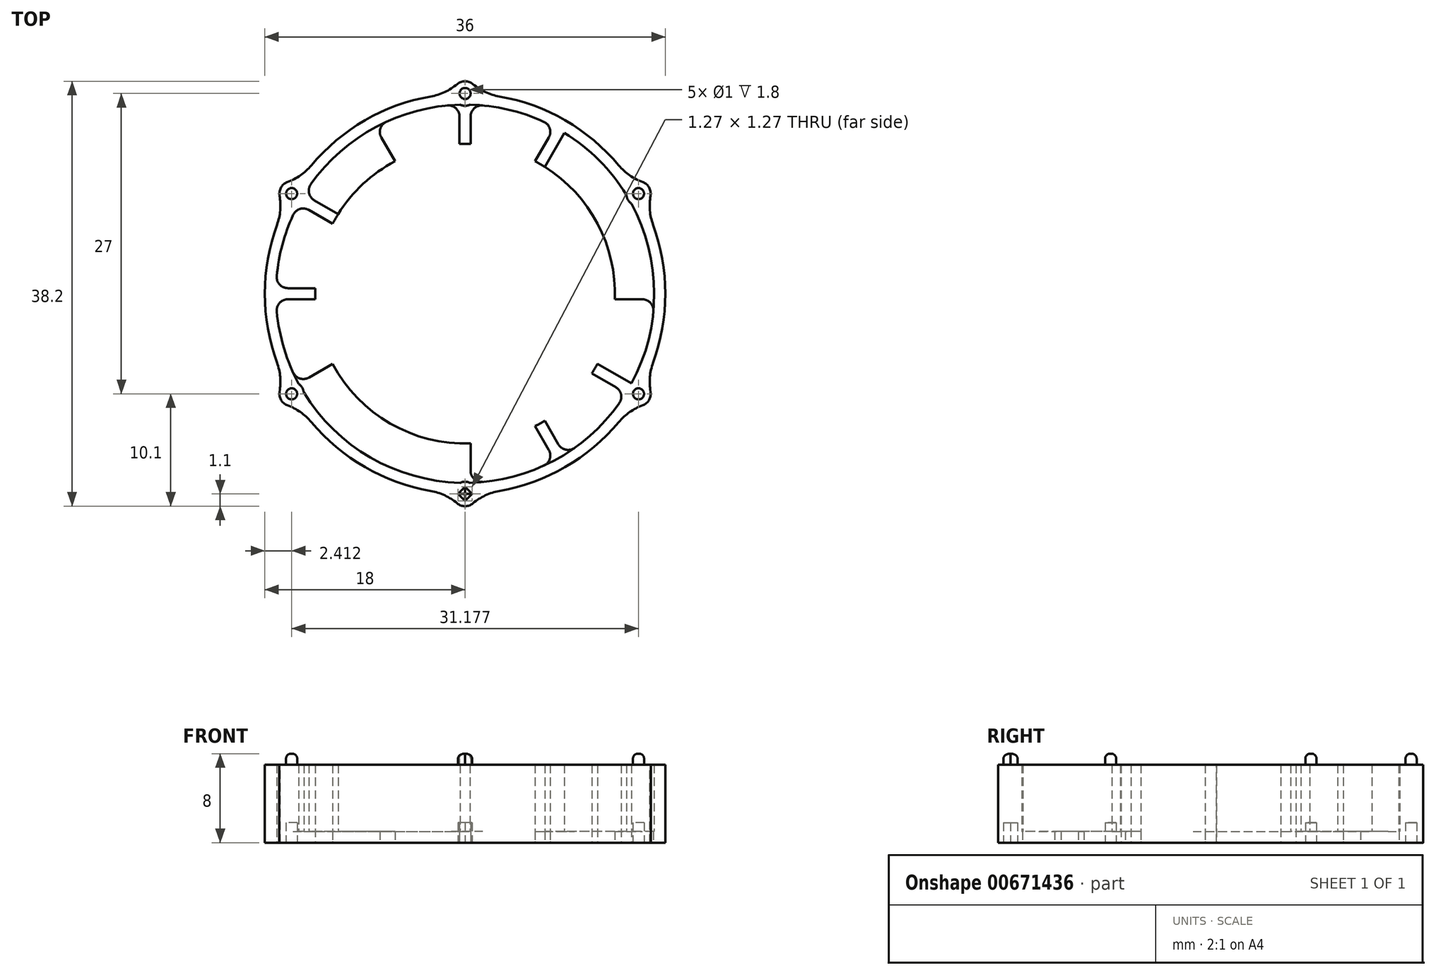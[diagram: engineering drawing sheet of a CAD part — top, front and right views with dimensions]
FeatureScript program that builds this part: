
annotation { "Feature Type Name" : "Feature", "Feature Type Description" : "" }
export const myFeature = defineFeature(function(context is Context, id is Id, definition is map)
    precondition{}
    {
        {
            var Q0;
            Q0=qCreatedBy(makeId("Top.planeOp"),FACE);
            var sketch = newSketch(context, id + "F0", { "sketchPlane" : qUnion([Q0])});
            skCircle(sketch, "E0", {"center": v(0, 0) * mm, "radius": 18 * mm});
            skCircle(sketch, "E1.0", {"center": v(0, 0) * mm, "radius": 17 * mm});
            skLineSegment(sketch, "E2.bottom", {"start": v(8.56, 15.83) * mm, "end": v(9.43, 15.33) * mm});
            skLineSegment(sketch, "E2.top", {"start": v(-9.43, -15.33) * mm, "end": v(-8.56, -15.83) * mm});
            skLineSegment(sketch, "E2.left", {"start": v(8.56, 15.83) * mm, "end": v(-9.43, -15.33) * mm});
            skLineSegment(sketch, "E2.right", {"start": v(9.43, 15.33) * mm, "end": v(-8.56, -15.83) * mm});
            skLineSegment(sketch, "E3.bottom", {"start": v(15.33, 9.43) * mm, "end": v(15.83, 8.56) * mm});
            skLineSegment(sketch, "E3.top", {"start": v(-15.83, -8.56) * mm, "end": v(-15.33, -9.43) * mm});
            skLineSegment(sketch, "E3.left", {"start": v(15.33, 9.43) * mm, "end": v(-15.83, -8.56) * mm});
            skLineSegment(sketch, "E3.right", {"start": v(15.83, 8.56) * mm, "end": v(-15.33, -9.43) * mm});
            skLineSegment(sketch, "E4", {"start": v(-38.35, 0) * mm, "end": v(39.17, 0) * mm, "construction": true});
            skLineSegment(sketch, "E5", {"start": v(0, 42.5) * mm, "end": v(0, -42.47) * mm, "construction": true});
            skLineSegment(sketch, "E6.bottom", {"start": v(-18, 0.5) * mm, "end": v(18, 0.5) * mm});
            skLineSegment(sketch, "E6.top", {"start": v(-18, -0.5) * mm, "end": v(18, -0.5) * mm});
            skLineSegment(sketch, "E6.left", {"start": v(-18, 0.5) * mm, "end": v(-18, -0.5) * mm});
            skLineSegment(sketch, "E6.right", {"start": v(18, 0.5) * mm, "end": v(18, -0.5) * mm});
            skLineSegment(sketch, "E7.bottom", {"start": v(-15.33, 9.43) * mm, "end": v(15.83, -8.56) * mm});
            skLineSegment(sketch, "E7.top", {"start": v(-15.83, 8.56) * mm, "end": v(15.33, -9.43) * mm});
            skLineSegment(sketch, "E7.left", {"start": v(-15.33, 9.43) * mm, "end": v(-15.83, 8.56) * mm});
            skLineSegment(sketch, "E7.right", {"start": v(15.83, -8.56) * mm, "end": v(15.33, -9.43) * mm});
            skLineSegment(sketch, "E8.bottom", {"start": v(-0.5, 18) * mm, "end": v(0.5, 18) * mm});
            skLineSegment(sketch, "E8.top", {"start": v(-0.5, -18) * mm, "end": v(0.5, -18) * mm});
            skLineSegment(sketch, "E8.left", {"start": v(-0.5, 18) * mm, "end": v(-0.5, -18) * mm});
            skLineSegment(sketch, "E8.right", {"start": v(0.5, 18) * mm, "end": v(0.5, -18) * mm});
            skLineSegment(sketch, "E9.bottom", {"start": v(-9.43, 15.33) * mm, "end": v(-8.56, 15.83) * mm});
            skLineSegment(sketch, "E9.top", {"start": v(8.56, -15.83) * mm, "end": v(9.43, -15.33) * mm});
            skLineSegment(sketch, "E9.left", {"start": v(-9.43, 15.33) * mm, "end": v(8.56, -15.83) * mm});
            skLineSegment(sketch, "E9.right", {"start": v(-8.56, 15.83) * mm, "end": v(9.43, -15.33) * mm});
            skCircle(sketch, "E10", {"center": v(0, 0) * mm, "radius": 13.47 * mm});
            skSolve(sketch);
        }
        {
            var Q0;
            Q0=qCreatedBy(makeId("Top.planeOp"),FACE);
            var sketch = newSketch(context, id + "F1", { "sketchPlane" : qUnion([Q0])});
            skCircle(sketch, "E11", {"center": v(0, 0) * mm, "radius": 18 * mm});
            skCircle(sketch, "E12", {"center": v(0, 0) * mm, "radius": 17 * mm});
            skSolve(sketch);
        }
        {
            var Q0;
            Q0=makeQuery(id+"F1.imprint","IMPRINT",FACE,{"disambiguationData":[TD([[makeQuery(id+"F1.imprint","IMPRINT",EDGE,{"derivedFrom":sQuery(id+"F1.wireOp",EDGE,"E11")}),1.0]])]});
            extrude(context, id + "F2", {"entities" : qUnion([Q0]), "depth" : 7 * mm, "offsetDistance" : 25 * mm});
        }
        {
            var Q0;
            {var subQ0=sQuery(id+"F0.wireOp",EDGE,"E7.bottom");var subQ1=sQuery(id+"F0.wireOp",EDGE,"E1.0");var subQ2=makeQuery(id+"F0.imprint","INTERSECT",VERTEX,{"disambiguationData":[OD(0.0)],"derivedFrom":[subQ1,subQ0]});Q0=makeQuery(id+"F0.imprint","IMPRINT",FACE,{"disambiguationData":[TD([[makeQuery(id+"F0.imprint","IMPRINT",EDGE,{"disambiguationData":[TD([[subQ2,-1.0]])],"derivedFrom":subQ1}),1.0]])]});}
            var Q1;
            {var subQ0=sQuery(id+"F0.wireOp",EDGE,"E2.right");var subQ1=sQuery(id+"F0.wireOp",EDGE,"E1.0");var subQ2=makeQuery(id+"F0.imprint","INTERSECT",VERTEX,{"disambiguationData":[OD(0.0)],"derivedFrom":[subQ1,subQ0]});Q1=makeQuery(id+"F0.imprint","IMPRINT",FACE,{"disambiguationData":[TD([[makeQuery(id+"F0.imprint","IMPRINT",EDGE,{"disambiguationData":[TD([[subQ2,-1.0]])],"derivedFrom":subQ1}),1.0]])]});}
            var Q2;
            {var subQ0=sQuery(id+"F0.wireOp",EDGE,"E7.top");var subQ1=sQuery(id+"F0.wireOp",EDGE,"E1.0");var subQ2=makeQuery(id+"F0.imprint","INTERSECT",VERTEX,{"disambiguationData":[OD(1.0)],"derivedFrom":[subQ1,subQ0]});Q2=makeQuery(id+"F0.imprint","IMPRINT",FACE,{"disambiguationData":[TD([[makeQuery(id+"F0.imprint","IMPRINT",EDGE,{"disambiguationData":[TD([[subQ2,-1.0]])],"derivedFrom":subQ1}),1.0]])]});}
            var Q3;
            {var subQ0=sQuery(id+"F0.wireOp",EDGE,"E6.bottom");var subQ1=sQuery(id+"F0.wireOp",EDGE,"E1.0");var subQ2=makeQuery(id+"F0.imprint","INTERSECT",VERTEX,{"disambiguationData":[OD(1.0)],"derivedFrom":[subQ1,subQ0]});Q3=makeQuery(id+"F0.imprint","IMPRINT",FACE,{"disambiguationData":[TD([[makeQuery(id+"F0.imprint","IMPRINT",EDGE,{"disambiguationData":[TD([[subQ2,-1.0]])],"derivedFrom":subQ1}),1.0]])]});}
            extrude(context, id + "F3", {"entities" : qUnion([Q0, Q1, Q2, Q3]), "operationType" : NewBodyOperationType.ADD, "depth" : 7 * mm, "offsetDistance" : 25 * mm});
        }
        {
            var Q0;
            Q0=makeQuery(id+"F1.imprint","IMPRINT",FACE,{"disambiguationData":[TD([[makeQuery(id+"F1.imprint","IMPRINT",EDGE,{"derivedFrom":sQuery(id+"F1.wireOp",EDGE,"E11")}),1.0]])]});
            var Q1;
            Q1=makeQuery(id+"F1.imprint","IMPRINT",FACE,{"disambiguationData":[TD([[makeQuery(id+"F1.imprint","IMPRINT",EDGE,{"derivedFrom":sQuery(id+"F1.wireOp",EDGE,"E12")}),1.0]])]});
            extrude(context, id + "F4", {"entities" : qUnion([Q0, Q1]), "operationType" : NewBodyOperationType.ADD, "depth" : 1 * mm, "offsetDistance" : 25 * mm});
        }
        {
            var Q0;
            Q0=qCreatedBy(makeId("Top.planeOp"),FACE);
            var sketch = newSketch(context, id + "F5", { "sketchPlane" : qUnion([Q0])});
            skCircle(sketch, "E13", {"center": v(0, 0) * mm, "radius": 18 * mm});
            skLineSegment(sketch, "E14", {"start": v(0, 18) * mm, "end": v(0, -18) * mm, "construction": true});
            skLineSegment(sketch, "E15", {"start": v(15.59, 9) * mm, "end": v(0, 0) * mm, "construction": true});
            skLineSegment(sketch, "E16", {"start": v(9, 15.59) * mm, "end": v(0, 0) * mm, "construction": true});
            skLineSegment(sketch, "E17", {"start": v(0, 0) * mm, "end": v(18, 0) * mm, "construction": true});
            skLineSegment(sketch, "E18", {"start": v(0, 0) * mm, "end": v(15.59, -9) * mm, "construction": true});
            skLineSegment(sketch, "E19", {"start": v(0, 0) * mm, "end": v(9, -15.59) * mm, "construction": true});
            skLineSegment(sketch, "E20", {"start": v(0, 0) * mm, "end": v(-9, 15.59) * mm, "construction": true});
            skLineSegment(sketch, "E21", {"start": v(0, 0) * mm, "end": v(-15.59, 9) * mm, "construction": true});
            skLineSegment(sketch, "E22", {"start": v(0, 0) * mm, "end": v(-18, 0) * mm, "construction": true});
            skLineSegment(sketch, "E23", {"start": v(0, 0) * mm, "end": v(-15.59, -9) * mm, "construction": true});
            skLineSegment(sketch, "E24", {"start": v(0, 0) * mm, "end": v(-9, -15.59) * mm, "construction": true});
            skCircle(sketch, "E25", {"center": v(0, 18) * mm, "radius": 1.1 * mm});
            skCircle(sketch, "E26", {"center": v(15.59, 9) * mm, "radius": 1.1 * mm});
            skCircle(sketch, "E27", {"center": v(15.59, -9) * mm, "radius": 1.1 * mm});
            skCircle(sketch, "E28", {"center": v(0, -18) * mm, "radius": 1.1 * mm});
            skCircle(sketch, "E29", {"center": v(-15.59, -9) * mm, "radius": 1.1 * mm});
            skCircle(sketch, "E30", {"center": v(-15.59, 9) * mm, "radius": 1.1 * mm});
            skCircle(sketch, "E31", {"center": v(-15.59, 9) * mm, "radius": 0.5 * mm});
            skCircle(sketch, "E32", {"center": v(0, 18) * mm, "radius": 0.5 * mm});
            skCircle(sketch, "E33", {"center": v(15.59, 9) * mm, "radius": 0.5 * mm});
            skCircle(sketch, "E34", {"center": v(15.59, -9) * mm, "radius": 0.5 * mm});
            skCircle(sketch, "E35", {"center": v(-15.59, -9) * mm, "radius": 0.5 * mm});
            skLineSegment(sketch, "E36.bottom", {"start": v(0.64, -18) * mm, "end": v(0, -18.64) * mm});
            skLineSegment(sketch, "E36.top", {"start": v(0, -17.36) * mm, "end": v(-0.64, -18) * mm});
            skLineSegment(sketch, "E36.left", {"start": v(0.64, -18) * mm, "end": v(0, -17.36) * mm});
            skLineSegment(sketch, "E36.right", {"start": v(0, -18.64) * mm, "end": v(-0.64, -18) * mm});
            skSolve(sketch);
        }
        {
            var Q0;
            {var subQ0=sQuery(id+"F5.wireOp",EDGE,"E30");var subQ1=sQuery(id+"F5.wireOp",EDGE,"E13");var subQ2=makeQuery(id+"F5.imprint","INTERSECT",VERTEX,{"disambiguationData":[OD(0.0)],"derivedFrom":[subQ1,subQ0]});Q0=makeQuery(id+"F5.imprint","IMPRINT",FACE,{"disambiguationData":[TD([[makeQuery(id+"F5.imprint","IMPRINT",EDGE,{"disambiguationData":[TD([[subQ2,-1.0]])],"derivedFrom":subQ1}),1.0]])]});}
            var Q1;
            {var subQ0=sQuery(id+"F5.wireOp",EDGE,"E30");var subQ1=sQuery(id+"F5.wireOp",EDGE,"E13");var subQ2=makeQuery(id+"F5.imprint","INTERSECT",VERTEX,{"disambiguationData":[OD(0.0)],"derivedFrom":[subQ1,subQ0]});Q1=makeQuery(id+"F5.imprint","IMPRINT",FACE,{"disambiguationData":[TD([[makeQuery(id+"F5.imprint","IMPRINT",EDGE,{"disambiguationData":[TD([[subQ2,-1.0]])],"derivedFrom":subQ1}),-1.0]])]});}
            var Q2;
            {var subQ0=sQuery(id+"F5.wireOp",EDGE,"E25");var subQ1=sQuery(id+"F5.wireOp",EDGE,"E13");var subQ2=makeQuery(id+"F5.imprint","INTERSECT",VERTEX,{"disambiguationData":[OD(0.0)],"derivedFrom":[subQ1,subQ0]});Q2=makeQuery(id+"F5.imprint","IMPRINT",FACE,{"disambiguationData":[TD([[makeQuery(id+"F5.imprint","IMPRINT",EDGE,{"disambiguationData":[TD([[subQ2,-1.0]])],"derivedFrom":subQ1}),1.0]])]});}
            var Q3;
            {var subQ0=sQuery(id+"F5.wireOp",EDGE,"E25");var subQ1=sQuery(id+"F5.wireOp",EDGE,"E13");var subQ2=makeQuery(id+"F5.imprint","INTERSECT",VERTEX,{"disambiguationData":[OD(0.0)],"derivedFrom":[subQ1,subQ0]});Q3=makeQuery(id+"F5.imprint","IMPRINT",FACE,{"disambiguationData":[TD([[makeQuery(id+"F5.imprint","IMPRINT",EDGE,{"disambiguationData":[TD([[subQ2,-1.0]])],"derivedFrom":subQ1}),-1.0]])]});}
            var Q4;
            {var subQ0=sQuery(id+"F5.wireOp",EDGE,"E26");var subQ1=sQuery(id+"F5.wireOp",EDGE,"E13");var subQ2=makeQuery(id+"F5.imprint","INTERSECT",VERTEX,{"disambiguationData":[OD(0.0)],"derivedFrom":[subQ1,subQ0]});Q4=makeQuery(id+"F5.imprint","IMPRINT",FACE,{"disambiguationData":[TD([[makeQuery(id+"F5.imprint","IMPRINT",EDGE,{"disambiguationData":[TD([[subQ2,-1.0]])],"derivedFrom":subQ1}),-1.0]])]});}
            var Q5;
            {var subQ0=sQuery(id+"F5.wireOp",EDGE,"E26");var subQ1=sQuery(id+"F5.wireOp",EDGE,"E13");var subQ2=makeQuery(id+"F5.imprint","INTERSECT",VERTEX,{"disambiguationData":[OD(0.0)],"derivedFrom":[subQ1,subQ0]});Q5=makeQuery(id+"F5.imprint","IMPRINT",FACE,{"disambiguationData":[TD([[makeQuery(id+"F5.imprint","IMPRINT",EDGE,{"disambiguationData":[TD([[subQ2,-1.0]])],"derivedFrom":subQ1}),1.0]])]});}
            var Q6;
            {var subQ0=sQuery(id+"F5.wireOp",EDGE,"E29");var subQ1=sQuery(id+"F5.wireOp",EDGE,"E13");var subQ2=makeQuery(id+"F5.imprint","INTERSECT",VERTEX,{"disambiguationData":[OD(0.0)],"derivedFrom":[subQ1,subQ0]});Q6=makeQuery(id+"F5.imprint","IMPRINT",FACE,{"disambiguationData":[TD([[makeQuery(id+"F5.imprint","IMPRINT",EDGE,{"disambiguationData":[TD([[subQ2,-1.0]])],"derivedFrom":subQ1}),1.0]])]});}
            var Q7;
            {var subQ0=sQuery(id+"F5.wireOp",EDGE,"E29");var subQ1=sQuery(id+"F5.wireOp",EDGE,"E13");var subQ2=makeQuery(id+"F5.imprint","INTERSECT",VERTEX,{"disambiguationData":[OD(0.0)],"derivedFrom":[subQ1,subQ0]});Q7=makeQuery(id+"F5.imprint","IMPRINT",FACE,{"disambiguationData":[TD([[makeQuery(id+"F5.imprint","IMPRINT",EDGE,{"disambiguationData":[TD([[subQ2,-1.0]])],"derivedFrom":subQ1}),-1.0]])]});}
            var Q8;
            {var subQ3=sQuery(id+"F5.wireOp",EDGE,"E13");var subQ5=sQuery(id+"F5.wireOp",EDGE,"E28");var subQ6=makeQuery(id+"F5.imprint","INTERSECT",VERTEX,{"disambiguationData":[OD(0.0)],"derivedFrom":[subQ3,subQ5]});Q8=makeQuery(id+"F5.imprint","IMPRINT",FACE,{"disambiguationData":[TD([[makeQuery(id+"F5.imprint","IMPRINT",EDGE,{"disambiguationData":[TD([[subQ6,-1.0]])],"derivedFrom":subQ3}),1.0]])]});}
            var Q9;
            {var subQ6=sQuery(id+"F5.wireOp",EDGE,"E36.bottom");Q9=makeQuery(id+"F5.imprint","IMPRINT",FACE,{"disambiguationData":[TD([[makeQuery(id+"F5.imprint","IMPRINT",EDGE,{"derivedFrom":subQ6}),1.0]])]});}
            var Q10;
            {var subQ0=sQuery(id+"F5.wireOp",EDGE,"E27");var subQ1=sQuery(id+"F5.wireOp",EDGE,"E13");var subQ2=makeQuery(id+"F5.imprint","INTERSECT",VERTEX,{"disambiguationData":[OD(0.0)],"derivedFrom":[subQ1,subQ0]});Q10=makeQuery(id+"F5.imprint","IMPRINT",FACE,{"disambiguationData":[TD([[makeQuery(id+"F5.imprint","IMPRINT",EDGE,{"disambiguationData":[TD([[subQ2,-1.0]])],"derivedFrom":subQ1}),-1.0]])]});}
            var Q11;
            {var subQ0=sQuery(id+"F5.wireOp",EDGE,"E27");var subQ1=sQuery(id+"F5.wireOp",EDGE,"E13");var subQ2=makeQuery(id+"F5.imprint","INTERSECT",VERTEX,{"disambiguationData":[OD(0.0)],"derivedFrom":[subQ1,subQ0]});Q11=makeQuery(id+"F5.imprint","IMPRINT",FACE,{"disambiguationData":[TD([[makeQuery(id+"F5.imprint","IMPRINT",EDGE,{"disambiguationData":[TD([[subQ2,-1.0]])],"derivedFrom":subQ1}),1.0]])]});}
            var Q12;
            {var subQ0=sQuery(id+"F5.wireOp",EDGE,"E31");var subQ1=sQuery(id+"F5.wireOp",EDGE,"E13");var subQ2=makeQuery(id+"F5.imprint","INTERSECT",VERTEX,{"disambiguationData":[OD(0.0)],"derivedFrom":[subQ1,subQ0]});Q12=makeQuery(id+"F5.imprint","IMPRINT",FACE,{"disambiguationData":[TD([[makeQuery(id+"F5.imprint","IMPRINT",EDGE,{"disambiguationData":[TD([[subQ2,-1.0]])],"derivedFrom":subQ1}),1.0]])]});}
            var Q13;
            {var subQ0=sQuery(id+"F5.wireOp",EDGE,"E31");var subQ1=sQuery(id+"F5.wireOp",EDGE,"E13");var subQ2=makeQuery(id+"F5.imprint","INTERSECT",VERTEX,{"disambiguationData":[OD(0.0)],"derivedFrom":[subQ1,subQ0]});Q13=makeQuery(id+"F5.imprint","IMPRINT",FACE,{"disambiguationData":[TD([[makeQuery(id+"F5.imprint","IMPRINT",EDGE,{"disambiguationData":[TD([[subQ2,-1.0]])],"derivedFrom":subQ1}),-1.0]])]});}
            var Q14;
            {var subQ0=sQuery(id+"F5.wireOp",EDGE,"E32");var subQ1=sQuery(id+"F5.wireOp",EDGE,"E13");var subQ2=makeQuery(id+"F5.imprint","INTERSECT",VERTEX,{"disambiguationData":[OD(0.0)],"derivedFrom":[subQ1,subQ0]});Q14=makeQuery(id+"F5.imprint","IMPRINT",FACE,{"disambiguationData":[TD([[makeQuery(id+"F5.imprint","IMPRINT",EDGE,{"disambiguationData":[TD([[subQ2,-1.0]])],"derivedFrom":subQ1}),-1.0]])]});}
            var Q15;
            {var subQ0=sQuery(id+"F5.wireOp",EDGE,"E32");var subQ1=sQuery(id+"F5.wireOp",EDGE,"E13");var subQ2=makeQuery(id+"F5.imprint","INTERSECT",VERTEX,{"disambiguationData":[OD(0.0)],"derivedFrom":[subQ1,subQ0]});Q15=makeQuery(id+"F5.imprint","IMPRINT",FACE,{"disambiguationData":[TD([[makeQuery(id+"F5.imprint","IMPRINT",EDGE,{"disambiguationData":[TD([[subQ2,-1.0]])],"derivedFrom":subQ1}),1.0]])]});}
            var Q16;
            {var subQ0=sQuery(id+"F5.wireOp",EDGE,"E33");var subQ1=sQuery(id+"F5.wireOp",EDGE,"E13");var subQ2=makeQuery(id+"F5.imprint","INTERSECT",VERTEX,{"disambiguationData":[OD(0.0)],"derivedFrom":[subQ1,subQ0]});Q16=makeQuery(id+"F5.imprint","IMPRINT",FACE,{"disambiguationData":[TD([[makeQuery(id+"F5.imprint","IMPRINT",EDGE,{"disambiguationData":[TD([[subQ2,-1.0]])],"derivedFrom":subQ1}),-1.0]])]});}
            var Q17;
            {var subQ0=sQuery(id+"F5.wireOp",EDGE,"E33");var subQ1=sQuery(id+"F5.wireOp",EDGE,"E13");var subQ2=makeQuery(id+"F5.imprint","INTERSECT",VERTEX,{"disambiguationData":[OD(0.0)],"derivedFrom":[subQ1,subQ0]});Q17=makeQuery(id+"F5.imprint","IMPRINT",FACE,{"disambiguationData":[TD([[makeQuery(id+"F5.imprint","IMPRINT",EDGE,{"disambiguationData":[TD([[subQ2,-1.0]])],"derivedFrom":subQ1}),1.0]])]});}
            var Q18;
            {var subQ0=sQuery(id+"F5.wireOp",EDGE,"E34");var subQ1=sQuery(id+"F5.wireOp",EDGE,"E13");var subQ2=makeQuery(id+"F5.imprint","INTERSECT",VERTEX,{"disambiguationData":[OD(0.0)],"derivedFrom":[subQ1,subQ0]});Q18=makeQuery(id+"F5.imprint","IMPRINT",FACE,{"disambiguationData":[TD([[makeQuery(id+"F5.imprint","IMPRINT",EDGE,{"disambiguationData":[TD([[subQ2,-1.0]])],"derivedFrom":subQ1}),-1.0]])]});}
            var Q19;
            {var subQ0=sQuery(id+"F5.wireOp",EDGE,"E34");var subQ1=sQuery(id+"F5.wireOp",EDGE,"E13");var subQ2=makeQuery(id+"F5.imprint","INTERSECT",VERTEX,{"disambiguationData":[OD(0.0)],"derivedFrom":[subQ1,subQ0]});Q19=makeQuery(id+"F5.imprint","IMPRINT",FACE,{"disambiguationData":[TD([[makeQuery(id+"F5.imprint","IMPRINT",EDGE,{"disambiguationData":[TD([[subQ2,-1.0]])],"derivedFrom":subQ1}),1.0]])]});}
            var Q20;
            {var subQ1=sQuery(id+"F5.wireOp",EDGE,"E36.bottom");Q20=makeQuery(id+"F5.imprint","IMPRINT",FACE,{"disambiguationData":[TD([[makeQuery(id+"F5.imprint","IMPRINT",EDGE,{"derivedFrom":subQ1}),-1.0]])]});}
            var Q21;
            {var subQ0=sQuery(id+"F5.wireOp",EDGE,"E35");var subQ1=sQuery(id+"F5.wireOp",EDGE,"E13");var subQ2=makeQuery(id+"F5.imprint","INTERSECT",VERTEX,{"disambiguationData":[OD(0.0)],"derivedFrom":[subQ1,subQ0]});Q21=makeQuery(id+"F5.imprint","IMPRINT",FACE,{"disambiguationData":[TD([[makeQuery(id+"F5.imprint","IMPRINT",EDGE,{"disambiguationData":[TD([[subQ2,-1.0]])],"derivedFrom":subQ1}),-1.0]])]});}
            var Q22;
            {var subQ0=sQuery(id+"F5.wireOp",EDGE,"E35");var subQ1=sQuery(id+"F5.wireOp",EDGE,"E13");var subQ2=makeQuery(id+"F5.imprint","INTERSECT",VERTEX,{"disambiguationData":[OD(0.0)],"derivedFrom":[subQ1,subQ0]});Q22=makeQuery(id+"F5.imprint","IMPRINT",FACE,{"disambiguationData":[TD([[makeQuery(id+"F5.imprint","IMPRINT",EDGE,{"disambiguationData":[TD([[subQ2,-1.0]])],"derivedFrom":subQ1}),1.0]])]});}
            var Q23;
            {var subQ0=sQuery(id+"F5.wireOp",EDGE,"E36.top");var subQ1=sQuery(id+"F5.wireOp",EDGE,"E13");var subQ2=makeQuery(id+"F5.imprint","INTERSECT",VERTEX,{"derivedFrom":[subQ1,subQ0]});Q23=makeQuery(id+"F5.imprint","IMPRINT",FACE,{"disambiguationData":[TD([[makeQuery(id+"F5.imprint","IMPRINT",EDGE,{"disambiguationData":[TD([[subQ2,-1.0]])],"derivedFrom":subQ1}),1.0]])]});}
            extrude(context, id + "F6", {"entities" : qUnion([Q0, Q1, Q2, Q3, Q4, Q5, Q6, Q7, Q8, Q9, Q10, Q11, Q12, Q13, Q14, Q15, Q16, Q17, Q18, Q19, Q20, Q21, Q22, Q23]), "operationType" : NewBodyOperationType.ADD, "depth" : 7 * mm, "offsetDistance" : 25 * mm});
        }
        {
            var Q0;
            {var subQ0=sQuery(id+"F0.wireOp",EDGE,"E8.right");var subQ1=sQuery(id+"F0.wireOp",EDGE,"E1.0");Q0=makeQuery(id+"F3.opExtrude","SWEPT_EDGE",EDGE,{"disambiguationData":[OSD([subQ1,subQ0]),TDD([makeQuery(id+"F0.imprint","INTERSECT",VERTEX,{"disambiguationData":[OD(1.0)],"derivedFrom":[subQ1,subQ0]})])]});}
            var Q1;
            {var subQ0=sQuery(id+"F0.wireOp",EDGE,"E2.left");var subQ1=sQuery(id+"F0.wireOp",EDGE,"E1.0");Q1=makeQuery(id+"F3.opExtrude","SWEPT_EDGE",EDGE,{"disambiguationData":[OSD([subQ1,subQ0]),TDD([makeQuery(id+"F0.imprint","INTERSECT",VERTEX,{"disambiguationData":[OD(1.0)],"derivedFrom":[subQ1,subQ0]})])]});}
            var Q2;
            {var subQ0=sQuery(id+"F0.wireOp",EDGE,"E3.left");var subQ1=sQuery(id+"F0.wireOp",EDGE,"E1.0");Q2=makeQuery(id+"F3.opExtrude","SWEPT_EDGE",EDGE,{"disambiguationData":[OSD([subQ1,subQ0]),TDD([makeQuery(id+"F0.imprint","INTERSECT",VERTEX,{"disambiguationData":[OD(1.0)],"derivedFrom":[subQ1,subQ0]})])]});}
            var Q3;
            {var subQ0=sQuery(id+"F0.wireOp",EDGE,"E6.bottom");var subQ1=sQuery(id+"F0.wireOp",EDGE,"E1.0");Q3=makeQuery(id+"F3.opExtrude","SWEPT_EDGE",EDGE,{"disambiguationData":[OSD([subQ1,subQ0]),TDD([makeQuery(id+"F0.imprint","INTERSECT",VERTEX,{"disambiguationData":[OD(1.0)],"derivedFrom":[subQ1,subQ0]})])]});}
            var Q4;
            {var subQ0=sQuery(id+"F0.wireOp",EDGE,"E9.right");var subQ1=sQuery(id+"F0.wireOp",EDGE,"E1.0");Q4=makeQuery(id+"F3.opExtrude","SWEPT_EDGE",EDGE,{"disambiguationData":[OSD([subQ1,subQ0]),TDD([makeQuery(id+"F0.imprint","INTERSECT",VERTEX,{"disambiguationData":[OD(1.0)],"derivedFrom":[subQ1,subQ0]})])]});}
            var Q5;
            {var subQ0=sQuery(id+"F0.wireOp",EDGE,"E7.bottom");var subQ1=sQuery(id+"F0.wireOp",EDGE,"E1.0");Q5=makeQuery(id+"F3.opExtrude","SWEPT_EDGE",EDGE,{"disambiguationData":[OSD([subQ1,subQ0]),TDD([makeQuery(id+"F0.imprint","INTERSECT",VERTEX,{"disambiguationData":[OD(1.0)],"derivedFrom":[subQ1,subQ0]})])]});}
            var Q6;
            {var subQ0=sQuery(id+"F0.wireOp",EDGE,"E8.left");var subQ1=sQuery(id+"F0.wireOp",EDGE,"E1.0");Q6=makeQuery(id+"F3.opExtrude","SWEPT_EDGE",EDGE,{"disambiguationData":[OSD([subQ1,subQ0]),TDD([makeQuery(id+"F0.imprint","INTERSECT",VERTEX,{"disambiguationData":[OD(0.0)],"derivedFrom":[subQ1,subQ0]})])]});}
            var Q7;
            {var subQ0=sQuery(id+"F0.wireOp",EDGE,"E2.left");var subQ1=sQuery(id+"F0.wireOp",EDGE,"E1.0");Q7=makeQuery(id+"F3.opExtrude","SWEPT_EDGE",EDGE,{"disambiguationData":[OSD([subQ1,subQ0]),TDD([makeQuery(id+"F0.imprint","INTERSECT",VERTEX,{"disambiguationData":[OD(0.0)],"derivedFrom":[subQ1,subQ0]})])]});}
            var Q8;
            {var subQ0=sQuery(id+"F0.wireOp",EDGE,"E3.left");var subQ1=sQuery(id+"F0.wireOp",EDGE,"E1.0");Q8=makeQuery(id+"F3.opExtrude","SWEPT_EDGE",EDGE,{"disambiguationData":[OSD([subQ1,subQ0]),TDD([makeQuery(id+"F0.imprint","INTERSECT",VERTEX,{"disambiguationData":[OD(0.0)],"derivedFrom":[subQ1,subQ0]})])]});}
            var Q9;
            {var subQ0=sQuery(id+"F0.wireOp",EDGE,"E6.top");var subQ1=sQuery(id+"F0.wireOp",EDGE,"E1.0");Q9=makeQuery(id+"F3.opExtrude","SWEPT_EDGE",EDGE,{"disambiguationData":[OSD([subQ1,subQ0]),TDD([makeQuery(id+"F0.imprint","INTERSECT",VERTEX,{"disambiguationData":[OD(1.0)],"derivedFrom":[subQ1,subQ0]})])]});}
            var Q10;
            {var subQ0=sQuery(id+"F0.wireOp",EDGE,"E7.top");var subQ1=sQuery(id+"F0.wireOp",EDGE,"E1.0");Q10=makeQuery(id+"F3.opExtrude","SWEPT_EDGE",EDGE,{"disambiguationData":[OSD([subQ1,subQ0]),TDD([makeQuery(id+"F0.imprint","INTERSECT",VERTEX,{"disambiguationData":[OD(0.0)],"derivedFrom":[subQ1,subQ0]})])]});}
            var Q11;
            {var subQ0=sQuery(id+"F0.wireOp",EDGE,"E6.top");var subQ1=sQuery(id+"F0.wireOp",EDGE,"E1.0");Q11=makeQuery(id+"F3.opExtrude","SWEPT_EDGE",EDGE,{"disambiguationData":[OSD([subQ1,subQ0]),TDD([makeQuery(id+"F0.imprint","INTERSECT",VERTEX,{"disambiguationData":[OD(0.0)],"derivedFrom":[subQ1,subQ0]})])]});}
            var Q12;
            {var subQ0=sQuery(id+"F0.wireOp",EDGE,"E9.left");var subQ1=sQuery(id+"F0.wireOp",EDGE,"E1.0");Q12=makeQuery(id+"F3.opExtrude","SWEPT_EDGE",EDGE,{"disambiguationData":[OSD([subQ1,subQ0]),TDD([makeQuery(id+"F0.imprint","INTERSECT",VERTEX,{"disambiguationData":[OD(0.0)],"derivedFrom":[subQ1,subQ0]})])]});}
            var Q13;
            {var subQ0=sQuery(id+"F0.wireOp",EDGE,"E8.right");var subQ1=sQuery(id+"F0.wireOp",EDGE,"E1.0");Q13=makeQuery(id+"F3.opExtrude","SWEPT_EDGE",EDGE,{"disambiguationData":[OSD([subQ1,subQ0]),TDD([makeQuery(id+"F0.imprint","INTERSECT",VERTEX,{"disambiguationData":[OD(0.0)],"derivedFrom":[subQ1,subQ0]})])]});}
            var Q14;
            {var subQ0=sQuery(id+"F0.wireOp",EDGE,"E7.bottom");var subQ1=sQuery(id+"F0.wireOp",EDGE,"E1.0");Q14=makeQuery(id+"F3.opExtrude","SWEPT_EDGE",EDGE,{"disambiguationData":[OSD([subQ1,subQ0]),TDD([makeQuery(id+"F0.imprint","INTERSECT",VERTEX,{"disambiguationData":[OD(0.0)],"derivedFrom":[subQ1,subQ0]})])]});}
            var Q15;
            {var subQ0=sQuery(id+"F0.wireOp",EDGE,"E9.right");var subQ1=sQuery(id+"F0.wireOp",EDGE,"E1.0");Q15=makeQuery(id+"F3.opExtrude","SWEPT_EDGE",EDGE,{"disambiguationData":[OSD([subQ1,subQ0]),TDD([makeQuery(id+"F0.imprint","INTERSECT",VERTEX,{"disambiguationData":[OD(0.0)],"derivedFrom":[subQ1,subQ0]})])]});}
            var Q16;
            {var subQ0=sQuery(id+"F0.wireOp",EDGE,"E3.right");var subQ1=sQuery(id+"F0.wireOp",EDGE,"E1.0");Q16=makeQuery(id+"F3.opExtrude","SWEPT_EDGE",EDGE,{"disambiguationData":[OSD([subQ1,subQ0]),TDD([makeQuery(id+"F0.imprint","INTERSECT",VERTEX,{"disambiguationData":[OD(1.0)],"derivedFrom":[subQ1,subQ0]})])]});}
            var Q17;
            {var subQ0=sQuery(id+"F0.wireOp",EDGE,"E2.right");var subQ1=sQuery(id+"F0.wireOp",EDGE,"E1.0");Q17=makeQuery(id+"F3.opExtrude","SWEPT_EDGE",EDGE,{"disambiguationData":[OSD([subQ1,subQ0]),TDD([makeQuery(id+"F0.imprint","INTERSECT",VERTEX,{"disambiguationData":[OD(1.0)],"derivedFrom":[subQ1,subQ0]})])]});}
            var Q18;
            {var subQ0=sQuery(id+"F0.wireOp",EDGE,"E3.right");var subQ1=sQuery(id+"F0.wireOp",EDGE,"E1.0");Q18=makeQuery(id+"F3.opExtrude","SWEPT_EDGE",EDGE,{"disambiguationData":[OSD([subQ1,subQ0]),TDD([makeQuery(id+"F0.imprint","INTERSECT",VERTEX,{"disambiguationData":[OD(0.0)],"derivedFrom":[subQ1,subQ0]})])]});}
            var Q19;
            {var subQ0=sQuery(id+"F0.wireOp",EDGE,"E2.right");var subQ1=sQuery(id+"F0.wireOp",EDGE,"E1.0");Q19=makeQuery(id+"F3.opExtrude","SWEPT_EDGE",EDGE,{"disambiguationData":[OSD([subQ1,subQ0]),TDD([makeQuery(id+"F0.imprint","INTERSECT",VERTEX,{"disambiguationData":[OD(0.0)],"derivedFrom":[subQ1,subQ0]})])]});}
            var Q20;
            {var subQ0=sQuery(id+"F0.wireOp",EDGE,"E8.left");var subQ1=sQuery(id+"F0.wireOp",EDGE,"E1.0");Q20=makeQuery(id+"F3.opExtrude","SWEPT_EDGE",EDGE,{"disambiguationData":[OSD([subQ1,subQ0]),TDD([makeQuery(id+"F0.imprint","INTERSECT",VERTEX,{"disambiguationData":[OD(1.0)],"derivedFrom":[subQ1,subQ0]})])]});}
            var Q21;
            {var subQ0=sQuery(id+"F0.wireOp",EDGE,"E9.left");var subQ1=sQuery(id+"F0.wireOp",EDGE,"E1.0");Q21=makeQuery(id+"F3.opExtrude","SWEPT_EDGE",EDGE,{"disambiguationData":[OSD([subQ1,subQ0]),TDD([makeQuery(id+"F0.imprint","INTERSECT",VERTEX,{"disambiguationData":[OD(1.0)],"derivedFrom":[subQ1,subQ0]})])]});}
            var Q22;
            {var subQ0=sQuery(id+"F0.wireOp",EDGE,"E7.top");var subQ1=sQuery(id+"F0.wireOp",EDGE,"E1.0");Q22=makeQuery(id+"F3.opExtrude","SWEPT_EDGE",EDGE,{"disambiguationData":[OSD([subQ1,subQ0]),TDD([makeQuery(id+"F0.imprint","INTERSECT",VERTEX,{"disambiguationData":[OD(1.0)],"derivedFrom":[subQ1,subQ0]})])]});}
            var Q23;
            {var subQ0=sQuery(id+"F0.wireOp",EDGE,"E6.bottom");var subQ1=sQuery(id+"F0.wireOp",EDGE,"E1.0");Q23=makeQuery(id+"F3.opExtrude","SWEPT_EDGE",EDGE,{"disambiguationData":[OSD([subQ1,subQ0]),TDD([makeQuery(id+"F0.imprint","INTERSECT",VERTEX,{"disambiguationData":[OD(0.0)],"derivedFrom":[subQ1,subQ0]})])]});}
            fillet(context, id + "F7", {"entities" : qUnion([Q0, Q1, Q2, Q3, Q4, Q5, Q6, Q7, Q8, Q9, Q10, Q11, Q12, Q13, Q14, Q15, Q16, Q17, Q18, Q19, Q20, Q21, Q22, Q23]), "radius" : 1 * mm, "tangentPropagation" : true, "allowEdgeOverflow" : false});
        }
        {
            var Q0;
            Q0=makeQuery(id+"F6.boolean.opBoolean","INTERSECT",EDGE,{"disambiguationData":[OD(0.0)],"derivedFrom":[makeQuery(id+"F2.opExtrude","SWEPT_FACE",FACE,{"disambiguationData":[OSD([sQuery(id+"F1.wireOp",EDGE,"E11")])]}),makeQuery(id+"F6.opExtrude","SWEPT_FACE",FACE,{"disambiguationData":[OSD([sQuery(id+"F5.wireOp",EDGE,"E30")])]})]});
            var Q1;
            Q1=makeQuery(id+"F6.boolean.opBoolean","INTERSECT",EDGE,{"disambiguationData":[OD(1.0)],"derivedFrom":[makeQuery(id+"F2.opExtrude","SWEPT_FACE",FACE,{"disambiguationData":[OSD([sQuery(id+"F1.wireOp",EDGE,"E11")])]}),makeQuery(id+"F6.opExtrude","SWEPT_FACE",FACE,{"disambiguationData":[OSD([sQuery(id+"F5.wireOp",EDGE,"E30")])]})]});
            var Q2;
            Q2=makeQuery(id+"F6.boolean.opBoolean","INTERSECT",EDGE,{"disambiguationData":[OD(1.0)],"derivedFrom":[makeQuery(id+"F2.opExtrude","SWEPT_FACE",FACE,{"disambiguationData":[OSD([sQuery(id+"F1.wireOp",EDGE,"E11")])]}),makeQuery(id+"F6.opExtrude","SWEPT_FACE",FACE,{"disambiguationData":[OSD([sQuery(id+"F5.wireOp",EDGE,"E25")])]})]});
            var Q3;
            Q3=makeQuery(id+"F6.boolean.opBoolean","INTERSECT",EDGE,{"disambiguationData":[OD(1.0)],"derivedFrom":[makeQuery(id+"F2.opExtrude","SWEPT_FACE",FACE,{"disambiguationData":[OSD([sQuery(id+"F1.wireOp",EDGE,"E11")])]}),makeQuery(id+"F6.opExtrude","SWEPT_FACE",FACE,{"disambiguationData":[OSD([sQuery(id+"F5.wireOp",EDGE,"E29")])]})]});
            var Q4;
            Q4=makeQuery(id+"F6.boolean.opBoolean","INTERSECT",EDGE,{"disambiguationData":[OD(0.0)],"derivedFrom":[makeQuery(id+"F2.opExtrude","SWEPT_FACE",FACE,{"disambiguationData":[OSD([sQuery(id+"F1.wireOp",EDGE,"E11")])]}),makeQuery(id+"F6.opExtrude","SWEPT_FACE",FACE,{"disambiguationData":[OSD([sQuery(id+"F5.wireOp",EDGE,"E29")])]})]});
            var Q5;
            Q5=makeQuery(id+"F6.boolean.opBoolean","INTERSECT",EDGE,{"disambiguationData":[OD(1.0)],"derivedFrom":[makeQuery(id+"F2.opExtrude","SWEPT_FACE",FACE,{"disambiguationData":[OSD([sQuery(id+"F1.wireOp",EDGE,"E11")])]}),makeQuery(id+"F6.opExtrude","SWEPT_FACE",FACE,{"disambiguationData":[OSD([sQuery(id+"F5.wireOp",EDGE,"E28")])]})]});
            var Q6;
            Q6=makeQuery(id+"F6.boolean.opBoolean","INTERSECT",EDGE,{"disambiguationData":[OD(0.0)],"derivedFrom":[makeQuery(id+"F2.opExtrude","SWEPT_FACE",FACE,{"disambiguationData":[OSD([sQuery(id+"F1.wireOp",EDGE,"E11")])]}),makeQuery(id+"F6.opExtrude","SWEPT_FACE",FACE,{"disambiguationData":[OSD([sQuery(id+"F5.wireOp",EDGE,"E28")])]})]});
            var Q7;
            Q7=makeQuery(id+"F6.boolean.opBoolean","INTERSECT",EDGE,{"disambiguationData":[OD(1.0)],"derivedFrom":[makeQuery(id+"F2.opExtrude","SWEPT_FACE",FACE,{"disambiguationData":[OSD([sQuery(id+"F1.wireOp",EDGE,"E11")])]}),makeQuery(id+"F6.opExtrude","SWEPT_FACE",FACE,{"disambiguationData":[OSD([sQuery(id+"F5.wireOp",EDGE,"E27")])]})]});
            var Q8;
            Q8=makeQuery(id+"F6.boolean.opBoolean","INTERSECT",EDGE,{"disambiguationData":[OD(0.0)],"derivedFrom":[makeQuery(id+"F2.opExtrude","SWEPT_FACE",FACE,{"disambiguationData":[OSD([sQuery(id+"F1.wireOp",EDGE,"E11")])]}),makeQuery(id+"F6.opExtrude","SWEPT_FACE",FACE,{"disambiguationData":[OSD([sQuery(id+"F5.wireOp",EDGE,"E27")])]})]});
            var Q9;
            Q9=makeQuery(id+"F6.boolean.opBoolean","INTERSECT",EDGE,{"disambiguationData":[OD(1.0)],"derivedFrom":[makeQuery(id+"F2.opExtrude","SWEPT_FACE",FACE,{"disambiguationData":[OSD([sQuery(id+"F1.wireOp",EDGE,"E11")])]}),makeQuery(id+"F6.opExtrude","SWEPT_FACE",FACE,{"disambiguationData":[OSD([sQuery(id+"F5.wireOp",EDGE,"E26")])]})]});
            var Q10;
            Q10=makeQuery(id+"F6.boolean.opBoolean","INTERSECT",EDGE,{"disambiguationData":[OD(0.0)],"derivedFrom":[makeQuery(id+"F2.opExtrude","SWEPT_FACE",FACE,{"disambiguationData":[OSD([sQuery(id+"F1.wireOp",EDGE,"E11")])]}),makeQuery(id+"F6.opExtrude","SWEPT_FACE",FACE,{"disambiguationData":[OSD([sQuery(id+"F5.wireOp",EDGE,"E26")])]})]});
            var Q11;
            Q11=makeQuery(id+"F6.boolean.opBoolean","INTERSECT",EDGE,{"disambiguationData":[OD(0.0)],"derivedFrom":[makeQuery(id+"F2.opExtrude","SWEPT_FACE",FACE,{"disambiguationData":[OSD([sQuery(id+"F1.wireOp",EDGE,"E11")])]}),makeQuery(id+"F6.opExtrude","SWEPT_FACE",FACE,{"disambiguationData":[OSD([sQuery(id+"F5.wireOp",EDGE,"E25")])]})]});
            fillet(context, id + "F8", {"entities" : qUnion([Q0, Q1, Q2, Q3, Q4, Q5, Q6, Q7, Q8, Q9, Q10, Q11]), "radius" : 5 * mm, "tangentPropagation" : true, "allowEdgeOverflow" : false});
        }
        {
            var Q0;
            {var subQ0=sQuery(id+"F5.wireOp",EDGE,"E31");var subQ1=sQuery(id+"F5.wireOp",EDGE,"E13");var subQ2=makeQuery(id+"F5.imprint","INTERSECT",VERTEX,{"disambiguationData":[OD(0.0)],"derivedFrom":[subQ1,subQ0]});Q0=makeQuery(id+"F5.imprint","IMPRINT",FACE,{"disambiguationData":[TD([[makeQuery(id+"F5.imprint","IMPRINT",EDGE,{"disambiguationData":[TD([[subQ2,-1.0]])],"derivedFrom":subQ1}),-1.0]])]});}
            var Q1;
            {var subQ0=sQuery(id+"F5.wireOp",EDGE,"E31");var subQ1=sQuery(id+"F5.wireOp",EDGE,"E13");var subQ2=makeQuery(id+"F5.imprint","INTERSECT",VERTEX,{"disambiguationData":[OD(0.0)],"derivedFrom":[subQ1,subQ0]});Q1=makeQuery(id+"F5.imprint","IMPRINT",FACE,{"disambiguationData":[TD([[makeQuery(id+"F5.imprint","IMPRINT",EDGE,{"disambiguationData":[TD([[subQ2,-1.0]])],"derivedFrom":subQ1}),1.0]])]});}
            var Q2;
            {var subQ0=sQuery(id+"F5.wireOp",EDGE,"E32");var subQ1=sQuery(id+"F5.wireOp",EDGE,"E13");var subQ2=makeQuery(id+"F5.imprint","INTERSECT",VERTEX,{"disambiguationData":[OD(0.0)],"derivedFrom":[subQ1,subQ0]});Q2=makeQuery(id+"F5.imprint","IMPRINT",FACE,{"disambiguationData":[TD([[makeQuery(id+"F5.imprint","IMPRINT",EDGE,{"disambiguationData":[TD([[subQ2,-1.0]])],"derivedFrom":subQ1}),-1.0]])]});}
            var Q3;
            {var subQ0=sQuery(id+"F5.wireOp",EDGE,"E32");var subQ1=sQuery(id+"F5.wireOp",EDGE,"E13");var subQ2=makeQuery(id+"F5.imprint","INTERSECT",VERTEX,{"disambiguationData":[OD(0.0)],"derivedFrom":[subQ1,subQ0]});Q3=makeQuery(id+"F5.imprint","IMPRINT",FACE,{"disambiguationData":[TD([[makeQuery(id+"F5.imprint","IMPRINT",EDGE,{"disambiguationData":[TD([[subQ2,-1.0]])],"derivedFrom":subQ1}),1.0]])]});}
            var Q4;
            {var subQ0=sQuery(id+"F5.wireOp",EDGE,"E33");var subQ1=sQuery(id+"F5.wireOp",EDGE,"E13");var subQ2=makeQuery(id+"F5.imprint","INTERSECT",VERTEX,{"disambiguationData":[OD(0.0)],"derivedFrom":[subQ1,subQ0]});Q4=makeQuery(id+"F5.imprint","IMPRINT",FACE,{"disambiguationData":[TD([[makeQuery(id+"F5.imprint","IMPRINT",EDGE,{"disambiguationData":[TD([[subQ2,-1.0]])],"derivedFrom":subQ1}),1.0]])]});}
            var Q5;
            {var subQ0=sQuery(id+"F5.wireOp",EDGE,"E33");var subQ1=sQuery(id+"F5.wireOp",EDGE,"E13");var subQ2=makeQuery(id+"F5.imprint","INTERSECT",VERTEX,{"disambiguationData":[OD(0.0)],"derivedFrom":[subQ1,subQ0]});Q5=makeQuery(id+"F5.imprint","IMPRINT",FACE,{"disambiguationData":[TD([[makeQuery(id+"F5.imprint","IMPRINT",EDGE,{"disambiguationData":[TD([[subQ2,-1.0]])],"derivedFrom":subQ1}),-1.0]])]});}
            var Q6;
            {var subQ0=sQuery(id+"F5.wireOp",EDGE,"E34");var subQ1=sQuery(id+"F5.wireOp",EDGE,"E13");var subQ2=makeQuery(id+"F5.imprint","INTERSECT",VERTEX,{"disambiguationData":[OD(0.0)],"derivedFrom":[subQ1,subQ0]});Q6=makeQuery(id+"F5.imprint","IMPRINT",FACE,{"disambiguationData":[TD([[makeQuery(id+"F5.imprint","IMPRINT",EDGE,{"disambiguationData":[TD([[subQ2,-1.0]])],"derivedFrom":subQ1}),1.0]])]});}
            var Q7;
            {var subQ0=sQuery(id+"F5.wireOp",EDGE,"E34");var subQ1=sQuery(id+"F5.wireOp",EDGE,"E13");var subQ2=makeQuery(id+"F5.imprint","INTERSECT",VERTEX,{"disambiguationData":[OD(0.0)],"derivedFrom":[subQ1,subQ0]});Q7=makeQuery(id+"F5.imprint","IMPRINT",FACE,{"disambiguationData":[TD([[makeQuery(id+"F5.imprint","IMPRINT",EDGE,{"disambiguationData":[TD([[subQ2,-1.0]])],"derivedFrom":subQ1}),-1.0]])]});}
            var Q8;
            {var subQ1=sQuery(id+"F5.wireOp",EDGE,"E36.bottom");Q8=makeQuery(id+"F5.imprint","IMPRINT",FACE,{"disambiguationData":[TD([[makeQuery(id+"F5.imprint","IMPRINT",EDGE,{"derivedFrom":subQ1}),-1.0]])]});}
            var Q9;
            {var subQ0=sQuery(id+"F5.wireOp",EDGE,"E36.top");var subQ1=sQuery(id+"F5.wireOp",EDGE,"E13");var subQ2=makeQuery(id+"F5.imprint","INTERSECT",VERTEX,{"derivedFrom":[subQ1,subQ0]});Q9=makeQuery(id+"F5.imprint","IMPRINT",FACE,{"disambiguationData":[TD([[makeQuery(id+"F5.imprint","IMPRINT",EDGE,{"disambiguationData":[TD([[subQ2,-1.0]])],"derivedFrom":subQ1}),1.0]])]});}
            var Q10;
            {var subQ0=sQuery(id+"F5.wireOp",EDGE,"E35");var subQ1=sQuery(id+"F5.wireOp",EDGE,"E13");var subQ2=makeQuery(id+"F5.imprint","INTERSECT",VERTEX,{"disambiguationData":[OD(0.0)],"derivedFrom":[subQ1,subQ0]});Q10=makeQuery(id+"F5.imprint","IMPRINT",FACE,{"disambiguationData":[TD([[makeQuery(id+"F5.imprint","IMPRINT",EDGE,{"disambiguationData":[TD([[subQ2,-1.0]])],"derivedFrom":subQ1}),-1.0]])]});}
            var Q11;
            {var subQ0=sQuery(id+"F5.wireOp",EDGE,"E35");var subQ1=sQuery(id+"F5.wireOp",EDGE,"E13");var subQ2=makeQuery(id+"F5.imprint","INTERSECT",VERTEX,{"disambiguationData":[OD(0.0)],"derivedFrom":[subQ1,subQ0]});Q11=makeQuery(id+"F5.imprint","IMPRINT",FACE,{"disambiguationData":[TD([[makeQuery(id+"F5.imprint","IMPRINT",EDGE,{"disambiguationData":[TD([[subQ2,-1.0]])],"derivedFrom":subQ1}),1.0]])]});}
            extrude(context, id + "F9", {"entities" : qUnion([Q0, Q1, Q2, Q3, Q4, Q5, Q6, Q7, Q8, Q9, Q10, Q11]), "operationType" : NewBodyOperationType.ADD, "depth" : 8 * mm, "offsetDistance" : 25 * mm});
        }
        {
            var Q0;
            Q0=makeQuery(id+"F9.opExtrude","CAP_EDGE",EDGE,{"disambiguationData":[OSD([sQuery(id+"F5.wireOp",EDGE,"E35")])],"isStart":false});
            var Q1;
            Q1=makeQuery(id+"F9.opExtrude","CAP_FACE",FACE,{"disambiguationData":[OSD([sQuery(id+"F5.wireOp",EDGE,"E31")])],"isStart":false});
            var Q2;
            Q2=makeQuery(id+"F9.opExtrude","CAP_FACE",FACE,{"disambiguationData":[OSD([sQuery(id+"F5.wireOp",EDGE,"E32")])],"isStart":false});
            var Q3;
            Q3=makeQuery(id+"F9.opExtrude","CAP_FACE",FACE,{"disambiguationData":[OSD([sQuery(id+"F5.wireOp",EDGE,"E33")])],"isStart":false});
            var Q4;
            Q4=makeQuery(id+"F9.opExtrude","CAP_FACE",FACE,{"disambiguationData":[OSD([sQuery(id+"F5.wireOp",EDGE,"E34")])],"isStart":false});
            var Q5;
            Q5=makeQuery(id+"F9.opExtrude","CAP_EDGE",EDGE,{"disambiguationData":[OSD([sQuery(id+"F5.wireOp",EDGE,"E36.left")])],"isStart":false});
            var Q6;
            Q6=makeQuery(id+"F9.opExtrude","CAP_EDGE",EDGE,{"disambiguationData":[OSD([sQuery(id+"F5.wireOp",EDGE,"E36.right")])],"isStart":false});
            var Q7;
            Q7=makeQuery(id+"F9.opExtrude","CAP_EDGE",EDGE,{"disambiguationData":[OSD([sQuery(id+"F5.wireOp",EDGE,"E36.bottom")])],"isStart":false});
            var Q8;
            Q8=makeQuery(id+"F9.opExtrude","CAP_EDGE",EDGE,{"disambiguationData":[OSD([sQuery(id+"F5.wireOp",EDGE,"E36.top")])],"isStart":false});
            fillet(context, id + "F10", {"entities" : qUnion([Q0, Q1, Q2, Q3, Q4, Q5, Q6, Q7, Q8]), "radius" : .45 * mm, "tangentPropagation" : true, "allowEdgeOverflow" : false});
        }
        {
            var Q0;
            {var subQ0=sQuery(id+"F5.wireOp",EDGE,"E35");var subQ1=sQuery(id+"F5.wireOp",EDGE,"E13");var subQ2=makeQuery(id+"F5.imprint","INTERSECT",VERTEX,{"disambiguationData":[OD(0.0)],"derivedFrom":[subQ1,subQ0]});Q0=makeQuery(id+"F5.imprint","IMPRINT",FACE,{"disambiguationData":[TD([[makeQuery(id+"F5.imprint","IMPRINT",EDGE,{"disambiguationData":[TD([[subQ2,-1.0]])],"derivedFrom":subQ1}),-1.0]])]});}
            var Q1;
            {var subQ0=sQuery(id+"F5.wireOp",EDGE,"E35");var subQ1=sQuery(id+"F5.wireOp",EDGE,"E13");var subQ2=makeQuery(id+"F5.imprint","INTERSECT",VERTEX,{"disambiguationData":[OD(0.0)],"derivedFrom":[subQ1,subQ0]});Q1=makeQuery(id+"F5.imprint","IMPRINT",FACE,{"disambiguationData":[TD([[makeQuery(id+"F5.imprint","IMPRINT",EDGE,{"disambiguationData":[TD([[subQ2,-1.0]])],"derivedFrom":subQ1}),1.0]])]});}
            var Q2;
            {var subQ1=sQuery(id+"F5.wireOp",EDGE,"E36.bottom");Q2=makeQuery(id+"F5.imprint","IMPRINT",FACE,{"disambiguationData":[TD([[makeQuery(id+"F5.imprint","IMPRINT",EDGE,{"derivedFrom":subQ1}),-1.0]])]});}
            var Q3;
            {var subQ0=sQuery(id+"F5.wireOp",EDGE,"E36.top");var subQ1=sQuery(id+"F5.wireOp",EDGE,"E13");var subQ2=makeQuery(id+"F5.imprint","INTERSECT",VERTEX,{"derivedFrom":[subQ1,subQ0]});Q3=makeQuery(id+"F5.imprint","IMPRINT",FACE,{"disambiguationData":[TD([[makeQuery(id+"F5.imprint","IMPRINT",EDGE,{"disambiguationData":[TD([[subQ2,-1.0]])],"derivedFrom":subQ1}),1.0]])]});}
            var Q4;
            {var subQ0=sQuery(id+"F5.wireOp",EDGE,"E34");var subQ1=sQuery(id+"F5.wireOp",EDGE,"E13");var subQ2=makeQuery(id+"F5.imprint","INTERSECT",VERTEX,{"disambiguationData":[OD(0.0)],"derivedFrom":[subQ1,subQ0]});Q4=makeQuery(id+"F5.imprint","IMPRINT",FACE,{"disambiguationData":[TD([[makeQuery(id+"F5.imprint","IMPRINT",EDGE,{"disambiguationData":[TD([[subQ2,-1.0]])],"derivedFrom":subQ1}),1.0]])]});}
            var Q5;
            {var subQ0=sQuery(id+"F5.wireOp",EDGE,"E34");var subQ1=sQuery(id+"F5.wireOp",EDGE,"E13");var subQ2=makeQuery(id+"F5.imprint","INTERSECT",VERTEX,{"disambiguationData":[OD(0.0)],"derivedFrom":[subQ1,subQ0]});Q5=makeQuery(id+"F5.imprint","IMPRINT",FACE,{"disambiguationData":[TD([[makeQuery(id+"F5.imprint","IMPRINT",EDGE,{"disambiguationData":[TD([[subQ2,-1.0]])],"derivedFrom":subQ1}),-1.0]])]});}
            var Q6;
            {var subQ0=sQuery(id+"F5.wireOp",EDGE,"E33");var subQ1=sQuery(id+"F5.wireOp",EDGE,"E13");var subQ2=makeQuery(id+"F5.imprint","INTERSECT",VERTEX,{"disambiguationData":[OD(0.0)],"derivedFrom":[subQ1,subQ0]});Q6=makeQuery(id+"F5.imprint","IMPRINT",FACE,{"disambiguationData":[TD([[makeQuery(id+"F5.imprint","IMPRINT",EDGE,{"disambiguationData":[TD([[subQ2,-1.0]])],"derivedFrom":subQ1}),1.0]])]});}
            var Q7;
            {var subQ0=sQuery(id+"F5.wireOp",EDGE,"E33");var subQ1=sQuery(id+"F5.wireOp",EDGE,"E13");var subQ2=makeQuery(id+"F5.imprint","INTERSECT",VERTEX,{"disambiguationData":[OD(0.0)],"derivedFrom":[subQ1,subQ0]});Q7=makeQuery(id+"F5.imprint","IMPRINT",FACE,{"disambiguationData":[TD([[makeQuery(id+"F5.imprint","IMPRINT",EDGE,{"disambiguationData":[TD([[subQ2,-1.0]])],"derivedFrom":subQ1}),-1.0]])]});}
            var Q8;
            {var subQ0=sQuery(id+"F5.wireOp",EDGE,"E32");var subQ1=sQuery(id+"F5.wireOp",EDGE,"E13");var subQ2=makeQuery(id+"F5.imprint","INTERSECT",VERTEX,{"disambiguationData":[OD(0.0)],"derivedFrom":[subQ1,subQ0]});Q8=makeQuery(id+"F5.imprint","IMPRINT",FACE,{"disambiguationData":[TD([[makeQuery(id+"F5.imprint","IMPRINT",EDGE,{"disambiguationData":[TD([[subQ2,-1.0]])],"derivedFrom":subQ1}),1.0]])]});}
            var Q9;
            {var subQ0=sQuery(id+"F5.wireOp",EDGE,"E32");var subQ1=sQuery(id+"F5.wireOp",EDGE,"E13");var subQ2=makeQuery(id+"F5.imprint","INTERSECT",VERTEX,{"disambiguationData":[OD(0.0)],"derivedFrom":[subQ1,subQ0]});Q9=makeQuery(id+"F5.imprint","IMPRINT",FACE,{"disambiguationData":[TD([[makeQuery(id+"F5.imprint","IMPRINT",EDGE,{"disambiguationData":[TD([[subQ2,-1.0]])],"derivedFrom":subQ1}),-1.0]])]});}
            var Q10;
            {var subQ0=sQuery(id+"F5.wireOp",EDGE,"E31");var subQ1=sQuery(id+"F5.wireOp",EDGE,"E13");var subQ2=makeQuery(id+"F5.imprint","INTERSECT",VERTEX,{"disambiguationData":[OD(0.0)],"derivedFrom":[subQ1,subQ0]});Q10=makeQuery(id+"F5.imprint","IMPRINT",FACE,{"disambiguationData":[TD([[makeQuery(id+"F5.imprint","IMPRINT",EDGE,{"disambiguationData":[TD([[subQ2,-1.0]])],"derivedFrom":subQ1}),-1.0]])]});}
            var Q11;
            {var subQ0=sQuery(id+"F5.wireOp",EDGE,"E31");var subQ1=sQuery(id+"F5.wireOp",EDGE,"E13");var subQ2=makeQuery(id+"F5.imprint","INTERSECT",VERTEX,{"disambiguationData":[OD(0.0)],"derivedFrom":[subQ1,subQ0]});Q11=makeQuery(id+"F5.imprint","IMPRINT",FACE,{"disambiguationData":[TD([[makeQuery(id+"F5.imprint","IMPRINT",EDGE,{"disambiguationData":[TD([[subQ2,-1.0]])],"derivedFrom":subQ1}),1.0]])]});}
            extrude(context, id + "F11", {"entities" : qUnion([Q0, Q1, Q2, Q3, Q4, Q5, Q6, Q7, Q8, Q9, Q10, Q11]), "operationType" : NewBodyOperationType.REMOVE, "depth" : 1.8 * mm, "offsetDistance" : 25 * mm});
        }
        {
            var Q0;
            Q0=qCreatedBy(makeId("Top.planeOp"),FACE);
            var sketch = newSketch(context, id + "F12", { "sketchPlane" : qUnion([Q0])});
            skCircle(sketch, "E37", {"center": v(0, 0) * mm, "radius": 13.47 * mm});
            skSolve(sketch);
        }
        {
            var Q0;
            Q0=makeQuery(id+"F12.imprint","IMPRINT",FACE,{"disambiguationData":[TD([[makeQuery(id+"F12.imprint","IMPRINT",EDGE,{"derivedFrom":sQuery(id+"F12.wireOp",EDGE,"E37")}),1.0]])]});
            extrude(context, id + "F13", {"entities" : qUnion([Q0]), "operationType" : NewBodyOperationType.REMOVE, "depth" : 1 * mm, "offsetDistance" : 25 * mm});
        }
        {
            var Q0;
            {var subQ0=sQuery(id+"F0.wireOp",EDGE,"E8.right");var subQ1=sQuery(id+"F0.wireOp",EDGE,"E1.0");var subQ2=makeQuery(id+"F0.imprint","INTERSECT",VERTEX,{"disambiguationData":[OD(1.0)],"derivedFrom":[subQ1,subQ0]});Q0=makeQuery(id+"F0.imprint","IMPRINT",FACE,{"disambiguationData":[TD([[makeQuery(id+"F0.imprint","IMPRINT",EDGE,{"disambiguationData":[TD([[subQ2,-1.0]])],"derivedFrom":subQ1}),1.0]])]});}
            var Q1;
            {var subQ0=sQuery(id+"F0.wireOp",EDGE,"E9.right");var subQ1=sQuery(id+"F0.wireOp",EDGE,"E1.0");var subQ2=makeQuery(id+"F0.imprint","INTERSECT",VERTEX,{"disambiguationData":[OD(1.0)],"derivedFrom":[subQ1,subQ0]});Q1=makeQuery(id+"F0.imprint","IMPRINT",FACE,{"disambiguationData":[TD([[makeQuery(id+"F0.imprint","IMPRINT",EDGE,{"disambiguationData":[TD([[subQ2,-1.0]])],"derivedFrom":subQ1}),1.0]])]});}
            var Q2;
            {var subQ0=sQuery(id+"F0.wireOp",EDGE,"E7.bottom");var subQ1=sQuery(id+"F0.wireOp",EDGE,"E1.0");var subQ2=makeQuery(id+"F0.imprint","INTERSECT",VERTEX,{"disambiguationData":[OD(1.0)],"derivedFrom":[subQ1,subQ0]});Q2=makeQuery(id+"F0.imprint","IMPRINT",FACE,{"disambiguationData":[TD([[makeQuery(id+"F0.imprint","IMPRINT",EDGE,{"disambiguationData":[TD([[subQ2,-1.0]])],"derivedFrom":subQ1}),1.0]])]});}
            var Q3;
            {var subQ0=sQuery(id+"F0.wireOp",EDGE,"E2.left");var subQ1=sQuery(id+"F0.wireOp",EDGE,"E1.0");var subQ2=makeQuery(id+"F0.imprint","INTERSECT",VERTEX,{"disambiguationData":[OD(0.0)],"derivedFrom":[subQ1,subQ0]});Q3=makeQuery(id+"F0.imprint","IMPRINT",FACE,{"disambiguationData":[TD([[makeQuery(id+"F0.imprint","IMPRINT",EDGE,{"disambiguationData":[TD([[subQ2,-1.0]])],"derivedFrom":subQ1}),1.0]])]});}
            var Q4;
            {var subQ0=sQuery(id+"F0.wireOp",EDGE,"E8.left");var subQ1=sQuery(id+"F0.wireOp",EDGE,"E1.0");var subQ2=makeQuery(id+"F0.imprint","INTERSECT",VERTEX,{"disambiguationData":[OD(0.0)],"derivedFrom":[subQ1,subQ0]});Q4=makeQuery(id+"F0.imprint","IMPRINT",FACE,{"disambiguationData":[TD([[makeQuery(id+"F0.imprint","IMPRINT",EDGE,{"disambiguationData":[TD([[subQ2,-1.0]])],"derivedFrom":subQ1}),1.0]])]});}
            var Q5;
            {var subQ0=sQuery(id+"F0.wireOp",EDGE,"E7.top");var subQ1=sQuery(id+"F0.wireOp",EDGE,"E1.0");var subQ2=makeQuery(id+"F0.imprint","INTERSECT",VERTEX,{"disambiguationData":[OD(0.0)],"derivedFrom":[subQ1,subQ0]});Q5=makeQuery(id+"F0.imprint","IMPRINT",FACE,{"disambiguationData":[TD([[makeQuery(id+"F0.imprint","IMPRINT",EDGE,{"disambiguationData":[TD([[subQ2,-1.0]])],"derivedFrom":subQ1}),1.0]])]});}
            var Q6;
            {var subQ0=sQuery(id+"F0.wireOp",EDGE,"E6.top");var subQ1=sQuery(id+"F0.wireOp",EDGE,"E1.0");var subQ2=makeQuery(id+"F0.imprint","INTERSECT",VERTEX,{"disambiguationData":[OD(0.0)],"derivedFrom":[subQ1,subQ0]});Q6=makeQuery(id+"F0.imprint","IMPRINT",FACE,{"disambiguationData":[TD([[makeQuery(id+"F0.imprint","IMPRINT",EDGE,{"disambiguationData":[TD([[subQ2,-1.0]])],"derivedFrom":subQ1}),1.0]])]});}
            extrude(context, id + "F14", {"entities" : qUnion([Q0, Q1, Q2, Q3, Q4, Q5, Q6]), "operationType" : NewBodyOperationType.REMOVE, "depth" : 1 * mm, "offsetDistance" : 25 * mm});
        }
        {
            var Q0;
            {var subQ0=sQuery(id+"F0.wireOp",EDGE,"E6.top");var subQ1=sQuery(id+"F0.wireOp",EDGE,"E1.0");Q0=makeQuery(id+"F14.boolean.opBoolean","COPY",EDGE,{"derivedFrom":makeQuery(id+"F14.opExtrude","SWEPT_EDGE",EDGE,{"disambiguationData":[OSD([subQ1,subQ0]),TDD([makeQuery(id+"F0.imprint","INTERSECT",VERTEX,{"disambiguationData":[OD(0.0)],"derivedFrom":[subQ1,subQ0]})])]})});}
            var Q1;
            {var subQ0=sQuery(id+"F0.wireOp",EDGE,"E7.top");var subQ1=sQuery(id+"F0.wireOp",EDGE,"E1.0");Q1=makeQuery(id+"F14.boolean.opBoolean","COPY",EDGE,{"derivedFrom":makeQuery(id+"F14.opExtrude","SWEPT_EDGE",EDGE,{"disambiguationData":[OSD([subQ1,subQ0]),TDD([makeQuery(id+"F0.imprint","INTERSECT",VERTEX,{"disambiguationData":[OD(0.0)],"derivedFrom":[subQ1,subQ0]})])]})});}
            var Q2;
            {var subQ0=sQuery(id+"F0.wireOp",EDGE,"E8.right");var subQ1=sQuery(id+"F0.wireOp",EDGE,"E1.0");Q2=makeQuery(id+"F14.boolean.opBoolean","COPY",EDGE,{"derivedFrom":makeQuery(id+"F14.opExtrude","SWEPT_EDGE",EDGE,{"disambiguationData":[OSD([subQ1,subQ0]),TDD([makeQuery(id+"F0.imprint","INTERSECT",VERTEX,{"disambiguationData":[OD(0.0)],"derivedFrom":[subQ1,subQ0]})])]})});}
            var Q3;
            {var subQ0=sQuery(id+"F0.wireOp",EDGE,"E9.right");var subQ1=sQuery(id+"F0.wireOp",EDGE,"E1.0");Q3=makeQuery(id+"F14.boolean.opBoolean","COPY",EDGE,{"derivedFrom":makeQuery(id+"F14.opExtrude","SWEPT_EDGE",EDGE,{"disambiguationData":[OSD([subQ1,subQ0]),TDD([makeQuery(id+"F0.imprint","INTERSECT",VERTEX,{"disambiguationData":[OD(0.0)],"derivedFrom":[subQ1,subQ0]})])]})});}
            var Q4;
            Q4=makeQuery(id+"F14.boolean.opBoolean","COPY",EDGE,{"derivedFrom":makeQuery(id+"F14.opExtrude","SWEPT_EDGE",EDGE,{"disambiguationData":[OSD([sQuery(id+"F0.wireOp",EDGE,"E1.0"),sQuery(id+"F0.wireOp",EDGE,"E3.left")])]})});
            var Q5;
            {var subQ0=sQuery(id+"F0.wireOp",EDGE,"E8.right");var subQ1=sQuery(id+"F0.wireOp",EDGE,"E1.0");Q5=makeQuery(id+"F14.boolean.opBoolean","COPY",EDGE,{"derivedFrom":makeQuery(id+"F14.opExtrude","SWEPT_EDGE",EDGE,{"disambiguationData":[OSD([subQ1,subQ0]),TDD([makeQuery(id+"F0.imprint","INTERSECT",VERTEX,{"disambiguationData":[OD(1.0)],"derivedFrom":[subQ1,subQ0]})])]})});}
            var Q6;
            Q6=makeQuery(id+"F14.boolean.opBoolean","COPY",EDGE,{"derivedFrom":makeQuery(id+"F14.opExtrude","SWEPT_EDGE",EDGE,{"disambiguationData":[OSD([sQuery(id+"F0.wireOp",EDGE,"E1.0"),sQuery(id+"F0.wireOp",EDGE,"E6.bottom")])]})});
            var Q7;
            {var subQ0=sQuery(id+"F0.wireOp",EDGE,"E9.right");var subQ1=sQuery(id+"F0.wireOp",EDGE,"E1.0");Q7=makeQuery(id+"F14.boolean.opBoolean","COPY",EDGE,{"derivedFrom":makeQuery(id+"F14.opExtrude","SWEPT_EDGE",EDGE,{"disambiguationData":[OSD([subQ1,subQ0]),TDD([makeQuery(id+"F0.imprint","INTERSECT",VERTEX,{"disambiguationData":[OD(1.0)],"derivedFrom":[subQ1,subQ0]})])]})});}
            var Q8;
            Q8=makeQuery(id+"F14.boolean.opBoolean","COPY",EDGE,{"derivedFrom":makeQuery(id+"F14.opExtrude","SWEPT_EDGE",EDGE,{"disambiguationData":[OSD([sQuery(id+"F0.wireOp",EDGE,"E1.0"),sQuery(id+"F0.wireOp",EDGE,"E7.bottom")])]})});
            var Q9;
            {var subQ0=sQuery(id+"F0.wireOp",EDGE,"E6.top");var subQ1=sQuery(id+"F0.wireOp",EDGE,"E1.0");Q9=makeQuery(id+"F14.boolean.opBoolean","COPY",EDGE,{"derivedFrom":makeQuery(id+"F14.opExtrude","SWEPT_EDGE",EDGE,{"disambiguationData":[OSD([subQ1,subQ0]),TDD([makeQuery(id+"F0.imprint","INTERSECT",VERTEX,{"disambiguationData":[OD(1.0)],"derivedFrom":[subQ1,subQ0]})])]})});}
            var Q10;
            Q10=makeQuery(id+"F14.boolean.opBoolean","COPY",EDGE,{"derivedFrom":makeQuery(id+"F14.opExtrude","SWEPT_EDGE",EDGE,{"disambiguationData":[OSD([sQuery(id+"F0.wireOp",EDGE,"E1.0"),sQuery(id+"F0.wireOp",EDGE,"E8.left")])]})});
            var Q11;
            Q11=makeQuery(id+"F14.boolean.opBoolean","COPY",EDGE,{"derivedFrom":makeQuery(id+"F14.opExtrude","SWEPT_EDGE",EDGE,{"disambiguationData":[OSD([sQuery(id+"F0.wireOp",EDGE,"E1.0"),sQuery(id+"F0.wireOp",EDGE,"E2.left")])]})});
            var Q12;
            {var subQ0=sQuery(id+"F0.wireOp",EDGE,"E7.top");var subQ1=sQuery(id+"F0.wireOp",EDGE,"E1.0");Q12=makeQuery(id+"F14.boolean.opBoolean","COPY",EDGE,{"derivedFrom":makeQuery(id+"F14.opExtrude","SWEPT_EDGE",EDGE,{"disambiguationData":[OSD([subQ1,subQ0]),TDD([makeQuery(id+"F0.imprint","INTERSECT",VERTEX,{"disambiguationData":[OD(1.0)],"derivedFrom":[subQ1,subQ0]})])]})});}
            var Q13;
            Q13=makeQuery(id+"F14.boolean.opBoolean","COPY",EDGE,{"derivedFrom":makeQuery(id+"F14.opExtrude","SWEPT_EDGE",EDGE,{"disambiguationData":[OSD([sQuery(id+"F0.wireOp",EDGE,"E1.0"),sQuery(id+"F0.wireOp",EDGE,"E9.left")])]})});
            fillet(context, id + "F15", {"entities" : qUnion([Q0, Q1, Q2, Q3, Q4, Q5, Q6, Q7, Q8, Q9, Q10, Q11, Q12, Q13]), "radius" : 1 * mm, "tangentPropagation" : true, "allowEdgeOverflow" : false});
        }
    });
